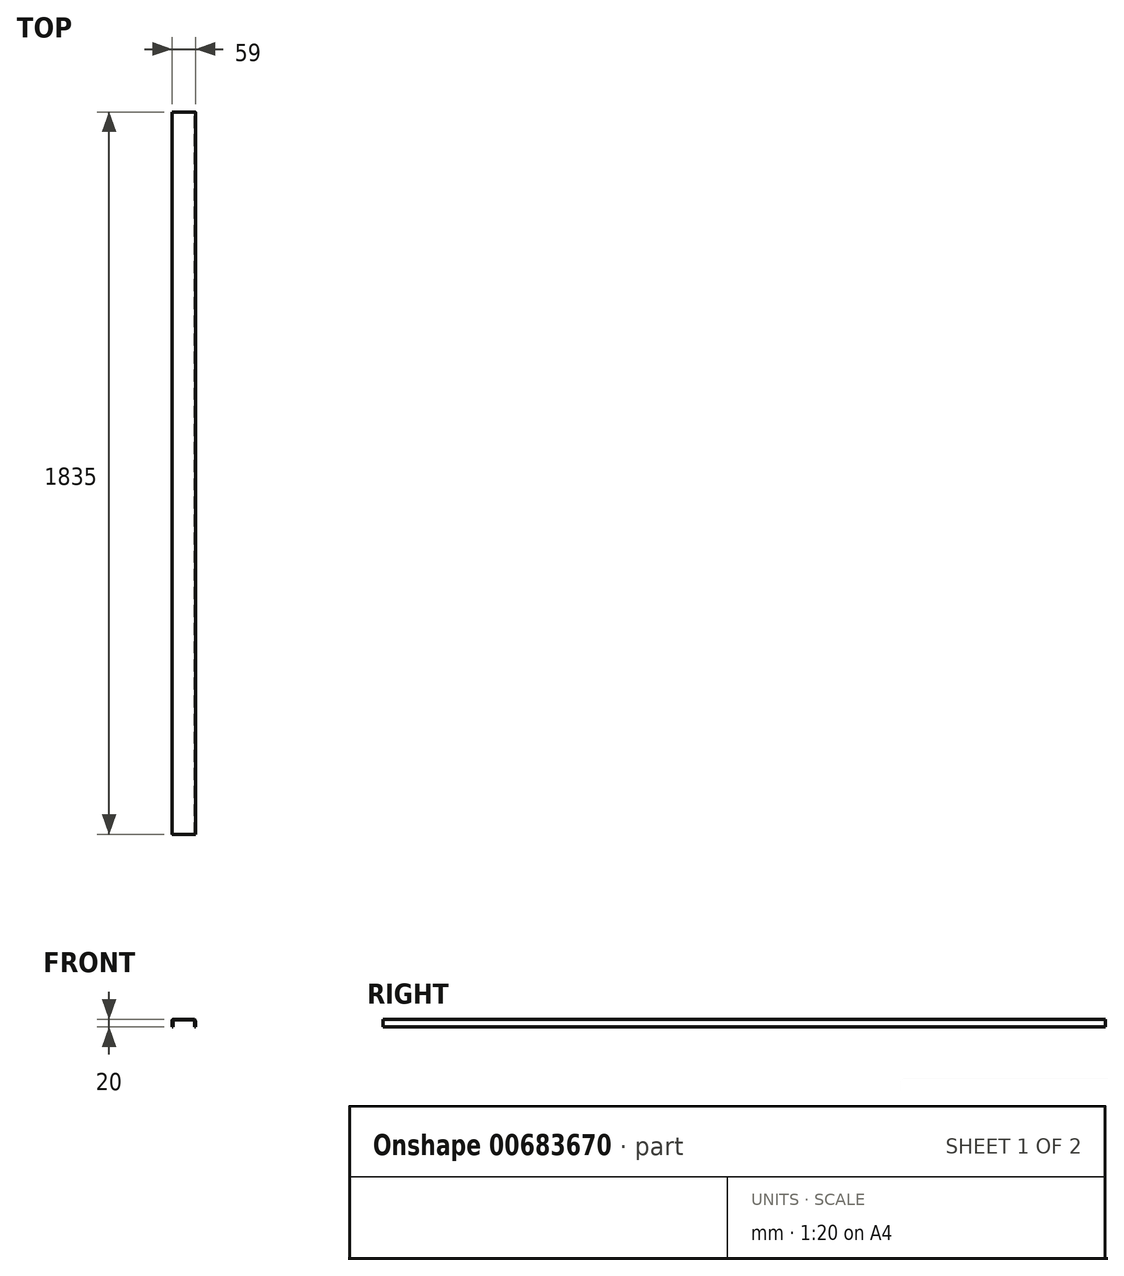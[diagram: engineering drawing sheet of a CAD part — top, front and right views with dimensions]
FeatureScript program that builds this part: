
annotation { "Feature Type Name" : "Feature", "Feature Type Description" : "" }
export const myFeature = defineFeature(function(context is Context, id is Id, definition is map)
    precondition{}
    {
        {
            var Q0;
            Q0=qCreatedBy(makeId("Front.planeOp"),FACE);
            var sketch = newSketch(context, id + "F0", { "sketchPlane" : qUnion([Q0])});
            skLineSegment(sketch, "E0.bottom", {"start": v(0, 0) * mm, "end": v(2, 0) * mm});
            skLineSegment(sketch, "E0.top", {"start": v(4, 20) * mm, "end": v(55, 20) * mm});
            skLineSegment(sketch, "E0.left", {"start": v(0, 0) * mm, "end": v(0, 16) * mm});
            skLineSegment(sketch, "E0.right", {"start": v(59, 0) * mm, "end": v(59, 16) * mm});
            skLineSegment(sketch, "E1.0", {"start": v(2, 0) * mm, "end": v(2, 16) * mm});
            skLineSegment(sketch, "E2.0", {"start": v(57, 0) * mm, "end": v(57, 16) * mm});
            skLineSegment(sketch, "E2.1", {"start": v(4, 18) * mm, "end": v(55, 18) * mm});
            skLineSegment(sketch, "E3.trimOffspring", {"start": v(57, 0) * mm, "end": v(59, 0) * mm});
            skArc(sketch, "E4.filletArc", {"start": v(4, 18) * mm, "mid": v(2.59, 17.41) * mm, "end": v(2, 16) * mm});
            skPoint(sketch, "E5.visualSharp", {"position": v(57, 18) * mm});
            skArc(sketch, "E5.filletArc", {"start": v(57, 16) * mm, "mid": v(56.41, 17.41) * mm, "end": v(55, 18) * mm});
            skPoint(sketch, "E6.visualSharp", {"position": v(0, 20) * mm});
            skArc(sketch, "E6.filletArc", {"start": v(4, 20) * mm, "mid": v(1.17, 18.83) * mm, "end": v(0, 16) * mm});
            skPoint(sketch, "E7.visualSharp", {"position": v(59, 20) * mm});
            skArc(sketch, "E7.filletArc", {"start": v(59, 16) * mm, "mid": v(57.83, 18.83) * mm, "end": v(55, 20) * mm});
            skSolve(sketch);
        }
        {
            var Q0;
            Q0=makeQuery(id+"F0.imprint","IMPRINT",FACE,{"disambiguationData":[TD([[makeQuery(id+"F0.imprint","IMPRINT",EDGE,{"derivedFrom":sQuery(id+"F0.wireOp",EDGE,"E0.bottom")}),1.0]])]});
            extrude(context, id + "F1", {"entities" : qUnion([Q0]), "depth" : 1835 * mm, "offsetDistance" : 25 * mm});
        }
    });
